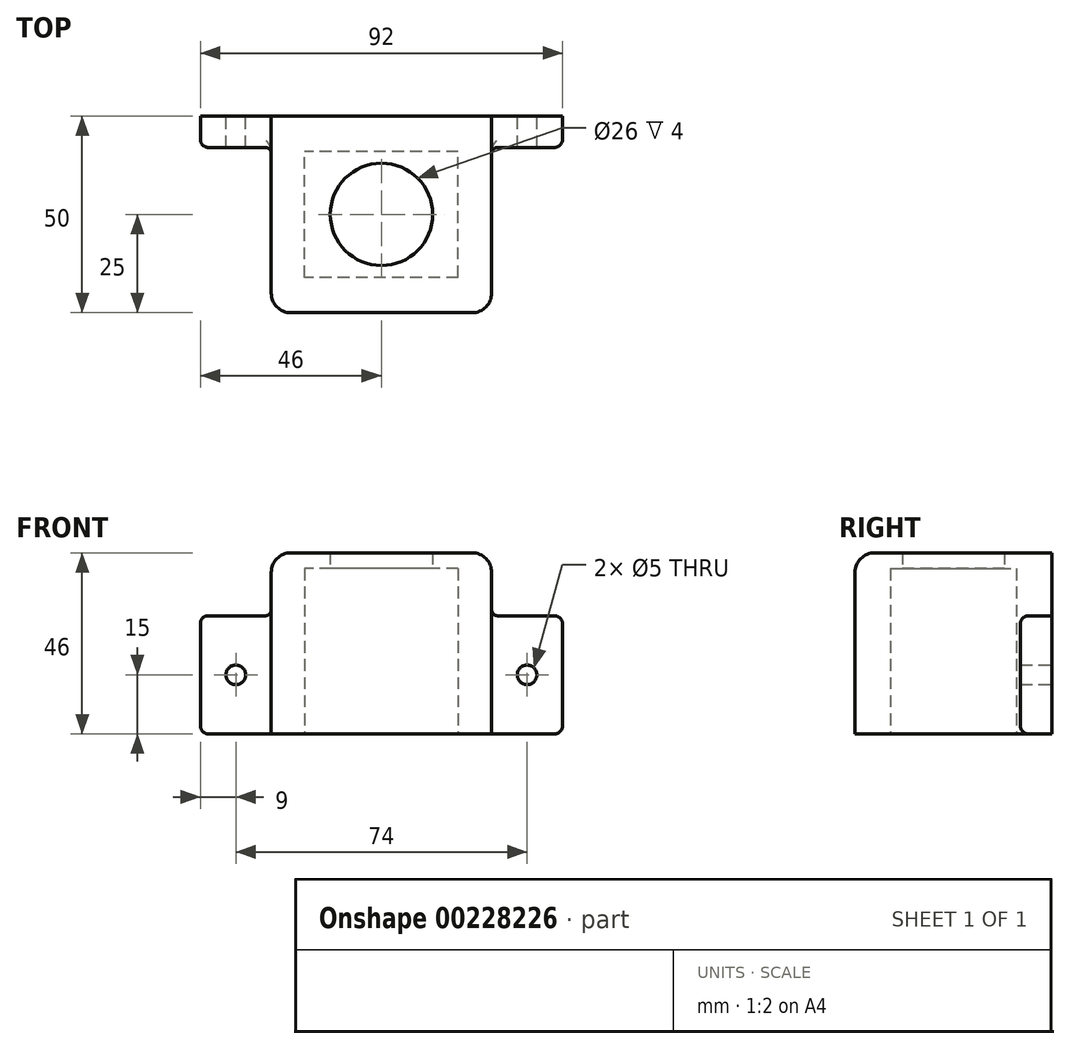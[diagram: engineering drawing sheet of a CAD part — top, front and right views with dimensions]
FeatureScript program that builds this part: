
annotation { "Feature Type Name" : "Feature", "Feature Type Description" : "" }
export const myFeature = defineFeature(function(context is Context, id is Id, definition is map)
    precondition{}
    {
        {
            var Q0;
            Q0=qCreatedBy(makeId("Top.planeOp"),FACE);
            var sketch = newSketch(context, id + "F0", { "sketchPlane" : qUnion([Q0])});
            skLineSegment(sketch, "E0.bottom", {"start": v(28, -25) * mm, "end": v(-28, -25) * mm});
            skLineSegment(sketch, "E0.top", {"start": v(28, 25) * mm, "end": v(-28, 25) * mm});
            skLineSegment(sketch, "E0.left", {"start": v(28, -25) * mm, "end": v(28, 25) * mm});
            skLineSegment(sketch, "E0.right", {"start": v(-28, -25) * mm, "end": v(-28, 25) * mm});
            skPoint(sketch, "E0.middle", {"position": v(0, 0) * mm});
            skSolve(sketch);
        }
        {
            var Q0;
            Q0=makeQuery(id+"F0.imprint","IMPRINT",FACE,{"disambiguationData":[TD([[makeQuery(id+"F0.imprint","IMPRINT",EDGE,{"derivedFrom":sQuery(id+"F0.wireOp",EDGE,"E0.bottom")}),-1.0]])]});
            extrude(context, id + "F1", {"entities" : qUnion([Q0]), "depth" : 46 * mm});
        }
        {
            var Q0;
            Q0=qCreatedBy(makeId("Top.planeOp"),FACE);
            var sketch = newSketch(context, id + "F2", { "sketchPlane" : qUnion([Q0])});
            skCircle(sketch, "E1", {"center": v(0, 0) * mm, "radius": 13 * mm});
            skSolve(sketch);
        }
        {
            var Q0;
            Q0 = qSketchRegion(id + "F2", true);
            extrude(context, id + "F3", {"entities" : qUnion([Q0]), "depth" : 50 * mm});
        }
        {
            var Q0;
            Q0=makeQuery(id+"F3.opExtrude","SWEPT_BODY",BODY,{"disambiguationData":[OSD([sQuery(id+"F2.wireOp",EDGE,"E1")])]});
            var Q1;
            Q1=makeQuery(id+"F1.opExtrude","SWEPT_BODY",BODY,{"disambiguationData":[OSD([sQuery(id+"F0.wireOp",EDGE,"E0.bottom"),sQuery(id+"F0.wireOp",EDGE,"E0.top"),sQuery(id+"F0.wireOp",EDGE,"E0.left"),sQuery(id+"F0.wireOp",EDGE,"E0.right")])]});
            booleanBodies(context, id + "F4", {"operationType" : BooleanOperationType.SUBTRACTION, "tools" : qUnion([Q0]), "targets" : qUnion([Q1])});
        }
        {
            var Q0;
            Q0=makeQuery(id+"F1.opExtrude","CAP_EDGE",EDGE,{"disambiguationData":[OSD([sQuery(id+"F0.wireOp",EDGE,"E0.right")])],"isStart":false});
            var Q1;
            Q1=makeQuery(id+"F1.opExtrude","CAP_EDGE",EDGE,{"disambiguationData":[OSD([sQuery(id+"F0.wireOp",EDGE,"E0.bottom")])],"isStart":false});
            var Q2;
            Q2=makeQuery(id+"F1.opExtrude","SWEPT_EDGE",EDGE,{"disambiguationData":[OSD([sQuery(id+"F0.wireOp",EDGE,"E0.bottom"),sQuery(id+"F0.wireOp",EDGE,"E0.right")])]});
            var Q3;
            Q3=makeQuery(id+"F1.opExtrude","SWEPT_EDGE",EDGE,{"disambiguationData":[OSD([sQuery(id+"F0.wireOp",EDGE,"E0.bottom"),sQuery(id+"F0.wireOp",EDGE,"E0.left")])]});
            var Q4;
            Q4=makeQuery(id+"F1.opExtrude","CAP_EDGE",EDGE,{"disambiguationData":[OSD([sQuery(id+"F0.wireOp",EDGE,"E0.left")])],"isStart":false});
            fillet(context, id + "F5", {"entities" : qUnion([Q0, Q1, Q2, Q3, Q4]), "radius" : 5 * mm, "tangentPropagation" : true, "allowEdgeOverflow" : false});
        }
        {
            var Q0;
            Q0=qCreatedBy(makeId("Top.planeOp"),FACE);
            var sketch = newSketch(context, id + "F6", { "sketchPlane" : qUnion([Q0])});
            skLineSegment(sketch, "E2.bottom", {"start": v(19.5, -16) * mm, "end": v(-19.5, -16) * mm});
            skLineSegment(sketch, "E2.top", {"start": v(19.5, 16) * mm, "end": v(-19.5, 16) * mm});
            skLineSegment(sketch, "E2.left", {"start": v(19.5, -16) * mm, "end": v(19.5, 16) * mm});
            skLineSegment(sketch, "E2.right", {"start": v(-19.5, -16) * mm, "end": v(-19.5, 16) * mm});
            skPoint(sketch, "E2.middle", {"position": v(0, 0) * mm});
            skSolve(sketch);
        }
        {
            var Q0;
            Q0=makeQuery(id+"F6.imprint","IMPRINT",FACE,{"disambiguationData":[TD([[makeQuery(id+"F6.imprint","IMPRINT",EDGE,{"derivedFrom":sQuery(id+"F6.wireOp",EDGE,"E2.bottom")}),-1.0]])]});
            extrude(context, id + "F7", {"entities" : qUnion([Q0]), "depth" : 42 * mm});
        }
        {
            var Q0;
            Q0=makeQuery(id+"F7.opExtrude","SWEPT_BODY",BODY,{"disambiguationData":[OSD([sQuery(id+"F6.wireOp",EDGE,"E2.bottom"),sQuery(id+"F6.wireOp",EDGE,"E2.top"),sQuery(id+"F6.wireOp",EDGE,"E2.left"),sQuery(id+"F6.wireOp",EDGE,"E2.right")])]});
            var Q1;
            Q1=makeQuery(id+"F1.opExtrude","SWEPT_BODY",BODY,{"disambiguationData":[OSD([sQuery(id+"F0.wireOp",EDGE,"E0.bottom"),sQuery(id+"F0.wireOp",EDGE,"E0.top"),sQuery(id+"F0.wireOp",EDGE,"E0.left"),sQuery(id+"F0.wireOp",EDGE,"E0.right")])]});
            booleanBodies(context, id + "F8", {"operationType" : BooleanOperationType.SUBTRACTION, "tools" : qUnion([Q0]), "targets" : qUnion([Q1])});
        }
        {
            var Q0;
            Q0=qCreatedBy(makeId("Front.planeOp"),FACE);
            var sketch = newSketch(context, id + "F9", { "sketchPlane" : qUnion([Q0])});
            skLineSegment(sketch, "E3", {"start": v(0, 0) * mm, "end": v(-46, 0) * mm});
            skLineSegment(sketch, "E4", {"start": v(-46, 0) * mm, "end": v(-46, 30) * mm});
            skLineSegment(sketch, "E5", {"start": v(-46, 30) * mm, "end": v(46, 30) * mm});
            skLineSegment(sketch, "E6", {"start": v(0, 0) * mm, "end": v(46, 0) * mm});
            skLineSegment(sketch, "E7", {"start": v(46, 0) * mm, "end": v(46, 30) * mm});
            skSolve(sketch);
        }
        {
            var Q0;
            Q0=makeQuery(id+"F9.imprint","IMPRINT",FACE,{"disambiguationData":[TD([[makeQuery(id+"F9.imprint","IMPRINT",EDGE,{"derivedFrom":sQuery(id+"F9.wireOp",EDGE,"E3")}),-1.0]])]});
            extrude(context, id + "F10", {"entities" : qUnion([Q0]), "depth" : 8 * mm});
        }
        {
            var Q0;
            Q0=qCreatedBy(makeId("Front.planeOp"),FACE);
            var sketch = newSketch(context, id + "F11", { "sketchPlane" : qUnion([Q0])});
            skCircle(sketch, "E8", {"center": v(-37, 15) * mm, "radius": 2.5 * mm});
            skCircle(sketch, "E9", {"center": v(37, 15) * mm, "radius": 2.5 * mm});
            skSolve(sketch);
        }
        {
            var Q0;
            Q0=makeQuery(id+"F11.imprint","IMPRINT",FACE,{"disambiguationData":[TD([[makeQuery(id+"F11.imprint","IMPRINT",EDGE,{"derivedFrom":sQuery(id+"F11.wireOp",EDGE,"E8")}),1.0]])]});
            var Q1;
            Q1=makeQuery(id+"F11.imprint","IMPRINT",FACE,{"disambiguationData":[TD([[makeQuery(id+"F11.imprint","IMPRINT",EDGE,{"derivedFrom":sQuery(id+"F11.wireOp",EDGE,"E9")}),1.0]])]});
            extrude(context, id + "F12", {"entities" : qUnion([Q0, Q1]), "depth" : 25 * mm});
        }
        {
            var Q0;
            Q0=makeQuery(id+"F12.opExtrude","SWEPT_BODY",BODY,{"disambiguationData":[OSD([sQuery(id+"F11.wireOp",EDGE,"E8")])]});
            var Q1;
            Q1=makeQuery(id+"F12.opExtrude","SWEPT_BODY",BODY,{"disambiguationData":[OSD([sQuery(id+"F11.wireOp",EDGE,"E9")])]});
            var Q2;
            Q2=makeQuery(id+"F10.opExtrude","SWEPT_BODY",BODY,{"disambiguationData":[OSD([sQuery(id+"F9.wireOp",EDGE,"E3"),sQuery(id+"F9.wireOp",EDGE,"E4"),sQuery(id+"F9.wireOp",EDGE,"E5"),sQuery(id+"F9.wireOp",EDGE,"E6"),sQuery(id+"F9.wireOp",EDGE,"E7")])]});
            booleanBodies(context, id + "F13", {"operationType" : BooleanOperationType.SUBTRACTION, "tools" : qUnion([Q0, Q1]), "targets" : qUnion([Q2])});
        }
        {
            var Q0;
            Q0=makeQuery(id+"F10.opExtrude","SWEPT_BODY",BODY,{"disambiguationData":[OSD([sQuery(id+"F9.wireOp",EDGE,"E3"),sQuery(id+"F9.wireOp",EDGE,"E4"),sQuery(id+"F9.wireOp",EDGE,"E5"),sQuery(id+"F9.wireOp",EDGE,"E6"),sQuery(id+"F9.wireOp",EDGE,"E7")])]});
            transform(context, id + "F14", {"entities" : qUnion([Q0]), "transformType" : TransformType.TRANSLATION_3D, "dx" : 0 * mm, "dy" : 25 * mm, "dz" : 0 * mm, "makeCopy" : false});
        }
        {
            var Q0;
            Q0=makeQuery(id+"F10.opExtrude","SWEPT_EDGE",EDGE,{"disambiguationData":[OSD([sQuery(id+"F9.wireOp",EDGE,"E4"),sQuery(id+"F9.wireOp",EDGE,"E5")])]});
            var Q1;
            Q1=makeQuery(id+"F10.opExtrude","CAP_EDGE",EDGE,{"disambiguationData":[OSD([sQuery(id+"F9.wireOp",EDGE,"E5")])],"isStart":false});
            var Q2;
            Q2=makeQuery(id+"F10.opExtrude","CAP_EDGE",EDGE,{"disambiguationData":[OSD([sQuery(id+"F9.wireOp",EDGE,"E4")])],"isStart":false});
            var Q3;
            Q3=makeQuery(id+"F10.opExtrude","CAP_EDGE",EDGE,{"disambiguationData":[OSD([sQuery(id+"F9.wireOp",EDGE,"E3"),sQuery(id+"F9.wireOp",EDGE,"E6")])],"isStart":false});
            var Q4;
            Q4=makeQuery(id+"F10.opExtrude","SWEPT_EDGE",EDGE,{"disambiguationData":[OSD([sQuery(id+"F9.wireOp",EDGE,"E3"),sQuery(id+"F9.wireOp",EDGE,"E4")])]});
            var Q5;
            Q5=makeQuery(id+"F10.opExtrude","CAP_EDGE",EDGE,{"disambiguationData":[OSD([sQuery(id+"F9.wireOp",EDGE,"E7")])],"isStart":false});
            var Q6;
            Q6=makeQuery(id+"F10.opExtrude","SWEPT_EDGE",EDGE,{"disambiguationData":[OSD([sQuery(id+"F9.wireOp",EDGE,"E6"),sQuery(id+"F9.wireOp",EDGE,"E7")])]});
            var Q7;
            Q7=makeQuery(id+"F10.opExtrude","SWEPT_EDGE",EDGE,{"disambiguationData":[OSD([sQuery(id+"F9.wireOp",EDGE,"E5"),sQuery(id+"F9.wireOp",EDGE,"E7")])]});
            fillet(context, id + "F15", {"entities" : qUnion([Q0, Q1, Q2, Q3, Q4, Q5, Q6, Q7]), "radius" : 2 * mm, "tangentPropagation" : true, "allowEdgeOverflow" : false});
        }
        {
            var Q0;
            Q0=makeQuery(id+"F1.opExtrude","SWEPT_BODY",BODY,{"disambiguationData":[OSD([sQuery(id+"F0.wireOp",EDGE,"E0.bottom"),sQuery(id+"F0.wireOp",EDGE,"E0.top"),sQuery(id+"F0.wireOp",EDGE,"E0.left"),sQuery(id+"F0.wireOp",EDGE,"E0.right")])]});
            var Q1;
            Q1=makeQuery(id+"F10.opExtrude","SWEPT_BODY",BODY,{"disambiguationData":[OSD([sQuery(id+"F9.wireOp",EDGE,"E3"),sQuery(id+"F9.wireOp",EDGE,"E4"),sQuery(id+"F9.wireOp",EDGE,"E5"),sQuery(id+"F9.wireOp",EDGE,"E6"),sQuery(id+"F9.wireOp",EDGE,"E7")])]});
            booleanBodies(context, id + "F16", {"operationType" : BooleanOperationType.UNION, "tools" : qUnion([Q0, Q1])});
        }
        {
            var Q0;
            Q0=makeQuery(id+"F16.opBoolean","INTERSECT",EDGE,{"derivedFrom":[makeQuery(id+"F1.opExtrude","SWEPT_FACE",FACE,{"disambiguationData":[OSD([sQuery(id+"F0.wireOp",EDGE,"E0.right")])]}),makeQuery(id+"F10.opExtrude","CAP_FACE",FACE,{"disambiguationData":[OSD([sQuery(id+"F9.wireOp",EDGE,"E3"),sQuery(id+"F9.wireOp",EDGE,"E4"),sQuery(id+"F9.wireOp",EDGE,"E5"),sQuery(id+"F9.wireOp",EDGE,"E6"),sQuery(id+"F9.wireOp",EDGE,"E7")])],"isStart":false})]});
            var Q1;
            Q1=makeQuery(id+"F16.opBoolean","INTERSECT",EDGE,{"derivedFrom":[makeQuery(id+"F1.opExtrude","SWEPT_FACE",FACE,{"disambiguationData":[OSD([sQuery(id+"F0.wireOp",EDGE,"E0.left")])]}),makeQuery(id+"F10.opExtrude","CAP_FACE",FACE,{"disambiguationData":[OSD([sQuery(id+"F9.wireOp",EDGE,"E3"),sQuery(id+"F9.wireOp",EDGE,"E4"),sQuery(id+"F9.wireOp",EDGE,"E5"),sQuery(id+"F9.wireOp",EDGE,"E6"),sQuery(id+"F9.wireOp",EDGE,"E7")])],"isStart":false})]});
            fillet(context, id + "F17", {"entities" : qUnion([Q0, Q1]), "radius" : 1.5 * mm, "tangentPropagation" : true, "allowEdgeOverflow" : false});
        }
    });
